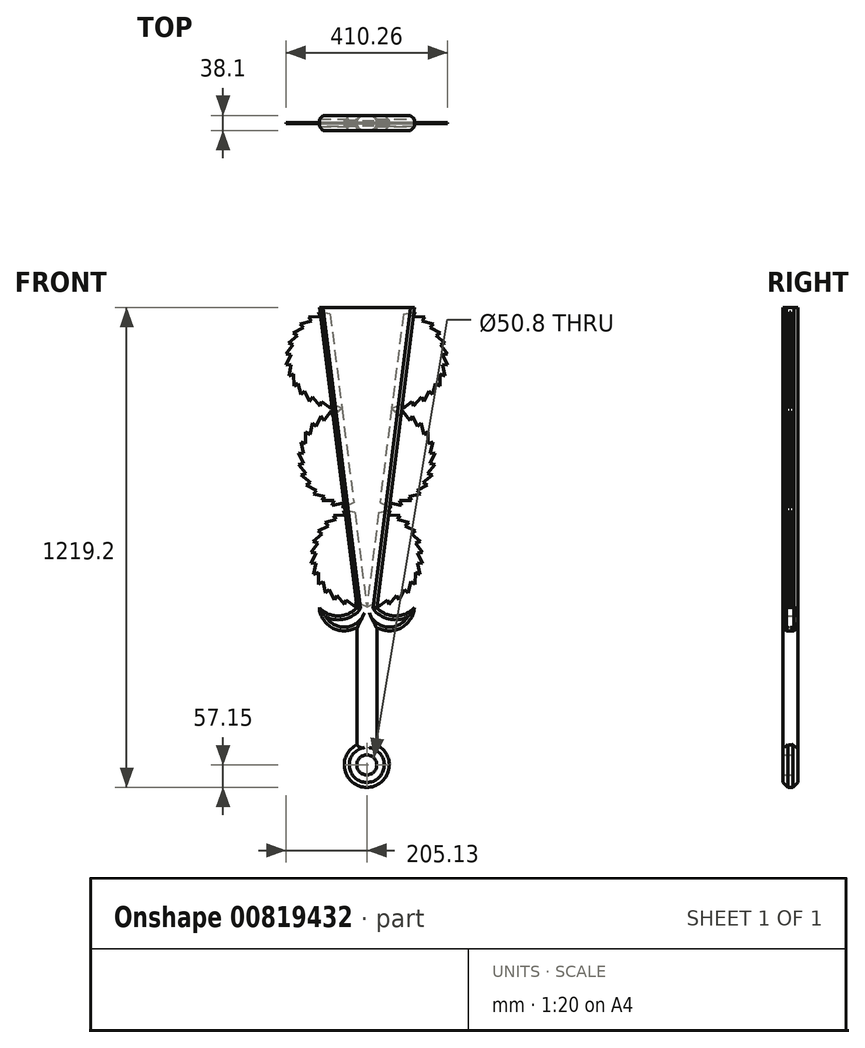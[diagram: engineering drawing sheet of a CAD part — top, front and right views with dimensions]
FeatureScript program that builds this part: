
annotation { "Feature Type Name" : "Feature", "Feature Type Description" : "" }
export const myFeature = defineFeature(function(context is Context, id is Id, definition is map)
    precondition{}
    {
        {
            var Q0;
            Q0=qCreatedBy(makeId("Front.planeOp"),FACE);
            var sketch = newSketch(context, id + "F0", { "sketchPlane" : qUnion([Q0])});
            skLineSegment(sketch, "E0.bottom", {"start": v(120.65, 0) * mm, "end": v(-120.65, 0) * mm});
            skLineSegment(sketch, "E0.top", {"start": v(120.65, 1219.2) * mm, "end": v(-120.65, 1219.2) * mm});
            skLineSegment(sketch, "E0.left", {"start": v(120.65, 0) * mm, "end": v(120.65, 1219.2) * mm});
            skLineSegment(sketch, "E0.right", {"start": v(-120.65, 0) * mm, "end": v(-120.65, 1219.2) * mm});
            skPoint(sketch, "E0.middle", {"position": v(0, 609.6) * mm});
            skLineSegment(sketch, "E1", {"start": v(-25.4, 457.2) * mm, "end": v(25.4, 457.2) * mm, "construction": true});
            skLineSegment(sketch, "E2.bottom", {"start": v(25.4, 457.2) * mm, "end": v(-25.4, 457.2) * mm, "construction": true});
            skLineSegment(sketch, "E2.top", {"start": v(25.4, 0) * mm, "end": v(-25.4, 0) * mm, "construction": true});
            skLineSegment(sketch, "E2.left", {"start": v(25.4, 457.2) * mm, "end": v(25.4, 0) * mm, "construction": true});
            skLineSegment(sketch, "E2.right", {"start": v(-25.4, 457.2) * mm, "end": v(-25.4, 0) * mm, "construction": true});
            skPoint(sketch, "E2.middle", {"position": v(0, 228.6) * mm});
            skArc(sketch, "E3", {"start": v(-25.4, 108.35) * mm, "mid": v(0, 0) * mm, "end": v(25.4, 108.35) * mm});
            skLineSegment(sketch, "E4", {"start": v(-25.4, 406.4) * mm, "end": v(-25.4, 108.35) * mm});
            skLineSegment(sketch, "E5", {"start": v(25.4, 406.4) * mm, "end": v(25.4, 108.35) * mm});
            skCircle(sketch, "E6", {"center": v(0, 57.15) * mm, "radius": 25.4 * mm});
            skPoint(sketch, "E7.end.orphan", {"position": v(120.65, 457.2) * mm});
            skLineSegment(sketch, "E8", {"start": v(-120.65, 1219.2) * mm, "end": v(-25.4, 457.2) * mm});
            skLineSegment(sketch, "E9", {"start": v(120.65, 1219.2) * mm, "end": v(25.4, 457.2) * mm});
            skLineSegment(sketch, "E10", {"start": v(-120.65, 457.2) * mm, "end": v(120.65, 457.2) * mm, "construction": true});
            skArc(sketch, "E11", {"start": v(25.4, 457.2) * mm, "mid": v(73.03, 435.7) * mm, "end": v(120.65, 457.2) * mm});
            skArc(sketch, "E12", {"start": v(120.65, 457.2) * mm, "mid": v(87.17, 405.29) * mm, "end": v(25.4, 406.4) * mm});
            skLineSegment(sketch, "E13", {"start": v(0, -278.18) * mm, "end": v(0, 1875.85) * mm, "construction": true});
            skArc(sketch, "E14.MirrorCS", {"start": v(-25.4, 457.2) * mm, "mid": v(-73.03, 435.7) * mm, "end": v(-120.65, 457.2) * mm});
            skArc(sketch, "E15.MirrorCS", {"start": v(-120.65, 457.2) * mm, "mid": v(-87.17, 405.29) * mm, "end": v(-25.4, 406.4) * mm});
            skSolve(sketch);
        }
        {
            var Q0;
            {var subQ1=sQuery(id+"F0.wireOp",EDGE,"E0.top");Q0=makeQuery(id+"F0.imprint","IMPRINT",FACE,{"disambiguationData":[TD([[makeQuery(id+"F0.imprint","IMPRINT",EDGE,{"derivedFrom":subQ1}),1.0]])]});}
            extrude(context, id + "F1", {"entities" : qUnion([Q0]), "depth" : 19.05 * mm, "offsetDistance" : 25.4 * mm, "hasSecondDirection" : true, "secondDirectionOppositeDirection" : true, "secondDirectionDepth" : 19.05 * mm});
        }
        {
            var Q0;
            Q0=makeQuery(id+"F0.imprint","IMPRINT",FACE,{"disambiguationData":[TD([[makeQuery(id+"F0.imprint","IMPRINT",EDGE,{"derivedFrom":sQuery(id+"F0.wireOp",EDGE,"E6")}),1.0]])]});
            extrude(context, id + "F2", {"entities" : qUnion([Q0]), "depth" : 19.05 * mm, "offsetDistance" : 25.4 * mm, "hasSecondDirection" : true, "secondDirectionOppositeDirection" : true, "secondDirectionDepth" : 19.05 * mm});
        }
        {
            var Q0;
            Q0=makeQuery(id+"F1.opExtrude","CAP_EDGE",EDGE,{"disambiguationData":[OSD([sQuery(id+"F0.wireOp",EDGE,"E4")])],"isStart":false});
            var Q1;
            Q1=makeQuery(id+"F1.opExtrude","CAP_EDGE",EDGE,{"disambiguationData":[OSD([sQuery(id+"F0.wireOp",EDGE,"E4")])],"isStart":true});
            var Q2;
            Q2=makeQuery(id+"F1.opExtrude","CAP_EDGE",EDGE,{"disambiguationData":[OSD([sQuery(id+"F0.wireOp",EDGE,"E5")])],"isStart":false});
            var Q3;
            Q3=makeQuery(id+"F1.opExtrude","CAP_EDGE",EDGE,{"disambiguationData":[OSD([sQuery(id+"F0.wireOp",EDGE,"E5")])],"isStart":true});
            fillet(context, id + "F3", {"entities" : qUnion([Q0, Q1, Q2, Q3]), "radius" : 19.05 * mm, "tangentPropagation" : true, "allowEdgeOverflow" : false});
        }
        {
            var Q0;
            Q0=makeQuery(id+"F1.opExtrude","CAP_EDGE",EDGE,{"disambiguationData":[OSD([sQuery(id+"F0.wireOp",EDGE,"E3")])],"isStart":false});
            var Q1;
            Q1=makeQuery(id+"F1.opExtrude","CAP_EDGE",EDGE,{"disambiguationData":[OSD([sQuery(id+"F0.wireOp",EDGE,"E3")])],"isStart":true});
            chamfer(context, id + "F4", {"entities" : qUnion([Q0, Q1]), "width" : 12.7 * mm, "tangentPropagation" : true});
        }
        {
            var Q0;
            Q0=qCreatedBy(makeId("Front.planeOp"),FACE);
            var sketch = newSketch(context, id + "F5", { "sketchPlane" : qUnion([Q0])});
            skLineSegment(sketch, "E16.bottom", {"start": v(120.65, 457.2) * mm, "end": v(-120.65, 457.2) * mm, "construction": true});
            skLineSegment(sketch, "E16.top", {"start": v(120.65, 1219.2) * mm, "end": v(-120.65, 1219.2) * mm, "construction": true});
            skLineSegment(sketch, "E16.left", {"start": v(120.65, 457.2) * mm, "end": v(120.65, 1219.2) * mm, "construction": true});
            skLineSegment(sketch, "E16.right", {"start": v(-120.65, 457.2) * mm, "end": v(-120.65, 1219.2) * mm, "construction": true});
            skPoint(sketch, "E16.middle", {"position": v(0, 838.2) * mm});
            skLineSegment(sketch, "E17", {"start": v(120.65, 1219.2) * mm, "end": v(25.4, 457.2) * mm, "construction": true});
            skLineSegment(sketch, "E18", {"start": v(-25.4, 457.2) * mm, "end": v(-120.65, 1219.2) * mm, "construction": true});
            skLineSegment(sketch, "E19", {"start": v(95.05, 1219.2) * mm, "end": v(-0.2, 457.2) * mm});
            skLineSegment(sketch, "E20", {"start": v(0.2, 457.2) * mm, "end": v(-95.05, 1219.2) * mm, "construction": true});
            skArc(sketch, "E21", {"start": v(0, 458.78) * mm, "mid": v(141.77, 569.05) * mm, "end": v(31.5, 710.82) * mm, "construction": true});
            skLineSegment(sketch, "E22", {"start": v(0, -215.51) * mm, "end": v(0, 1906.29) * mm, "construction": true});
            skArc(sketch, "E23", {"start": v(31.5, 710.82) * mm, "mid": v(173.28, 821.09) * mm, "end": v(63, 962.86) * mm, "construction": true});
            skArc(sketch, "E24", {"start": v(63, 962.86) * mm, "mid": v(204.78, 1073.13) * mm, "end": v(94.51, 1214.9) * mm, "construction": true});
            skPoint(sketch, "E25", {"position": v(0, 458.78) * mm});
            skLineSegment(sketch, "E26", {"start": v(15.75, 584.8) * mm, "end": v(120.65, 571.69) * mm, "construction": true});
            skLineSegment(sketch, "E27", {"start": v(47.26, 836.84) * mm, "end": v(173.28, 821.09) * mm, "construction": true});
            skLineSegment(sketch, "E28", {"start": v(78.76, 1088.88) * mm, "end": v(204.78, 1073.13) * mm, "construction": true});
            skLineSegment(sketch, "E29", {"start": v(15.75, 584.8) * mm, "end": v(120.65, 546.66) * mm, "construction": true});
            skLineSegment(sketch, "E30", {"start": v(15.75, 584.8) * mm, "end": v(39.44, 569.51) * mm, "construction": true});
            skLineSegment(sketch, "E31", {"start": v(104.46, 493.91) * mm, "end": v(95.59, 503) * mm});
            skLineSegment(sketch, "E32", {"start": v(82, 476.45) * mm, "end": v(75.38, 487.29) * mm});
            skLineSegment(sketch, "E33", {"start": v(56.24, 464.43) * mm, "end": v(52.2, 476.46) * mm});
            skLineSegment(sketch, "E34", {"start": v(28.44, 458.44) * mm, "end": v(27.15, 471.23) * mm});
            skLineSegment(sketch, "E35", {"start": v(142.12, 597.48) * mm, "end": v(129.48, 596.22) * mm});
            skLineSegment(sketch, "E36", {"start": v(136.13, 625.29) * mm, "end": v(124.09, 621.24) * mm});
            skLineSegment(sketch, "E37", {"start": v(124.1, 651.06) * mm, "end": v(113.27, 644.43) * mm});
            skLineSegment(sketch, "E38", {"start": v(106.64, 673.5) * mm, "end": v(97.55, 664.63) * mm});
            skLineSegment(sketch, "E39", {"start": v(84.62, 691.5) * mm, "end": v(77.74, 680.83) * mm});
            skLineSegment(sketch, "E40", {"start": v(59.15, 704.15) * mm, "end": v(54.81, 692.22) * mm});
            skLineSegment(sketch, "E41", {"start": v(31.5, 710.82) * mm, "end": v(258.62, 682.43) * mm, "construction": true});
            skLineSegment(sketch, "E42", {"start": v(63, 962.86) * mm, "end": v(273.36, 936.56) * mm, "construction": true});
            skLineSegment(sketch, "E43", {"start": v(52.2, 476.46) * mm, "end": v(28.44, 458.44) * mm});
            skLineSegment(sketch, "E44", {"start": v(75.38, 487.29) * mm, "end": v(56.24, 464.43) * mm});
            skLineSegment(sketch, "E45", {"start": v(95.59, 503) * mm, "end": v(82, 476.45) * mm});
            skLineSegment(sketch, "E46", {"start": v(111.79, 522.82) * mm, "end": v(104.46, 493.91) * mm});
            skLineSegment(sketch, "E47", {"start": v(123.17, 545.74) * mm, "end": v(122.46, 515.93) * mm});
            skLineSegment(sketch, "E48", {"start": v(129.17, 570.62) * mm, "end": v(135.1, 541.4) * mm});
            skLineSegment(sketch, "E49", {"start": v(129.48, 596.22) * mm, "end": v(141.77, 569.05) * mm});
            skLineSegment(sketch, "E50", {"start": v(124.09, 621.24) * mm, "end": v(142.12, 597.48) * mm});
            skLineSegment(sketch, "E51", {"start": v(113.27, 644.43) * mm, "end": v(136.13, 625.29) * mm});
            skLineSegment(sketch, "E52", {"start": v(97.55, 664.63) * mm, "end": v(124.1, 651.06) * mm});
            skLineSegment(sketch, "E53", {"start": v(77.74, 680.83) * mm, "end": v(106.64, 673.5) * mm});
            skLineSegment(sketch, "E54", {"start": v(54.81, 692.22) * mm, "end": v(84.62, 691.5) * mm});
            skLineSegment(sketch, "E55", {"start": v(29.93, 698.22) * mm, "end": v(59.15, 704.15) * mm});
            skLineSegment(sketch, "E56.trimOffspring", {"start": v(44.9, 613.25) * mm, "end": v(15.75, 584.8) * mm, "construction": true});
            skLineSegment(sketch, "E57.trimOffspring", {"start": v(47.5, 633.98) * mm, "end": v(15.75, 584.8) * mm, "construction": true});
            skLineSegment(sketch, "E58.trimOffspring", {"start": v(43.47, 601.75) * mm, "end": v(15.75, 584.8) * mm, "construction": true});
            skLineSegment(sketch, "E59.trimOffspring", {"start": v(120.65, 620.08) * mm, "end": v(15.75, 584.8) * mm, "construction": true});
            skLineSegment(sketch, "E60.trimOffspring", {"start": v(120.65, 595.33) * mm, "end": v(15.75, 584.8) * mm, "construction": true});
            skLineSegment(sketch, "E61.trimOffspring", {"start": v(129.17, 570.62) * mm, "end": v(141.77, 569.05) * mm});
            skLineSegment(sketch, "E62.trimOffspring", {"start": v(123.17, 545.74) * mm, "end": v(135.1, 541.4) * mm});
            skLineSegment(sketch, "E63.trimOffspring", {"start": v(111.79, 522.82) * mm, "end": v(122.46, 515.93) * mm});
            skLineSegment(sketch, "E64.trimOffspring", {"start": v(38.44, 561.55) * mm, "end": v(15.75, 584.8) * mm, "construction": true});
            skLineSegment(sketch, "E65.trimOffspring", {"start": v(37, 550.05) * mm, "end": v(15.75, 584.8) * mm, "construction": true});
            skLineSegment(sketch, "E66.trimOffspring", {"start": v(34.41, 529.32) * mm, "end": v(15.75, 584.8) * mm, "construction": true});
            skLineSegment(sketch, "E67", {"start": v(0, 458.78) * mm, "end": v(27.15, 471.23) * mm});
            skLineSegment(sketch, "E68.MirrorCS", {"start": v(63, 962.86) * mm, "end": v(86.26, 944.1) * mm});
            skLineSegment(sketch, "E69.MirrorCS", {"start": v(90.66, 956.2) * mm, "end": v(86.26, 944.1) * mm});
            skLineSegment(sketch, "E70.MirrorCS", {"start": v(116.13, 943.54) * mm, "end": v(109.24, 932.87) * mm});
            skLineSegment(sketch, "E71.MirrorCS", {"start": v(109.24, 932.87) * mm, "end": v(90.66, 956.2) * mm});
            skLineSegment(sketch, "E72.MirrorCS", {"start": v(129.06, 916.67) * mm, "end": v(116.13, 943.54) * mm});
            skLineSegment(sketch, "E73.MirrorCS", {"start": v(138.15, 925.54) * mm, "end": v(129.06, 916.67) * mm});
            skLineSegment(sketch, "E74.MirrorCS", {"start": v(144.77, 896.47) * mm, "end": v(138.15, 925.54) * mm});
            skLineSegment(sketch, "E75.MirrorCS", {"start": v(155.6, 903.1) * mm, "end": v(144.77, 896.47) * mm});
            skLineSegment(sketch, "E76.MirrorCS", {"start": v(155.6, 873.28) * mm, "end": v(155.6, 903.1) * mm});
            skLineSegment(sketch, "E77.MirrorCS", {"start": v(160.99, 848.25) * mm, "end": v(167.63, 877.32) * mm});
            skLineSegment(sketch, "E78.MirrorCS", {"start": v(160.99, 848.25) * mm, "end": v(173.62, 849.52) * mm});
            skLineSegment(sketch, "E79.MirrorCS", {"start": v(155.6, 873.28) * mm, "end": v(167.63, 877.32) * mm});
            skLineSegment(sketch, "E80.MirrorCS", {"start": v(160.67, 822.66) * mm, "end": v(173.62, 849.52) * mm});
            skLineSegment(sketch, "E81.MirrorCS", {"start": v(160.67, 822.66) * mm, "end": v(173.28, 821.09) * mm});
            skLineSegment(sketch, "E82.MirrorCS", {"start": v(154.68, 797.78) * mm, "end": v(173.28, 821.09) * mm});
            skLineSegment(sketch, "E83.MirrorCS", {"start": v(166.61, 793.44) * mm, "end": v(154.68, 797.78) * mm});
            skLineSegment(sketch, "E84.MirrorCS", {"start": v(143.3, 774.86) * mm, "end": v(166.61, 793.44) * mm});
            skLineSegment(sketch, "E85.MirrorCS", {"start": v(153.96, 767.97) * mm, "end": v(143.3, 774.86) * mm});
            skLineSegment(sketch, "E86.MirrorCS", {"start": v(127.1, 755.04) * mm, "end": v(153.96, 767.97) * mm});
            skLineSegment(sketch, "E87.MirrorCS", {"start": v(135.96, 745.95) * mm, "end": v(127.1, 755.04) * mm});
            skLineSegment(sketch, "E88.MirrorCS", {"start": v(106.89, 739.33) * mm, "end": v(135.96, 745.95) * mm});
            skLineSegment(sketch, "E89.MirrorCS", {"start": v(83.7, 728.5) * mm, "end": v(113.51, 728.5) * mm});
            skLineSegment(sketch, "E90.MirrorCS", {"start": v(58.67, 723.11) * mm, "end": v(87.74, 716.47) * mm});
            skLineSegment(sketch, "E91.MirrorCS", {"start": v(59.94, 710.47) * mm, "end": v(58.67, 723.11) * mm});
            skLineSegment(sketch, "E92.MirrorCS", {"start": v(33.08, 723.42) * mm, "end": v(59.94, 710.47) * mm});
            skLineSegment(sketch, "E93.MirrorCS", {"start": v(87.74, 716.47) * mm, "end": v(83.7, 728.5) * mm});
            skLineSegment(sketch, "E94.MirrorCS", {"start": v(113.51, 728.5) * mm, "end": v(106.89, 739.33) * mm});
            skLineSegment(sketch, "E95.MirrorCS", {"start": v(92.94, 1202.3) * mm, "end": v(122.16, 1208.23) * mm});
            skLineSegment(sketch, "E96.MirrorCS", {"start": v(122.16, 1208.23) * mm, "end": v(117.82, 1196.3) * mm});
            skLineSegment(sketch, "E97.MirrorCS", {"start": v(117.82, 1196.3) * mm, "end": v(147.63, 1195.58) * mm});
            skLineSegment(sketch, "E98.MirrorCS", {"start": v(140.75, 1184.91) * mm, "end": v(169.65, 1177.58) * mm});
            skLineSegment(sketch, "E99.MirrorCS", {"start": v(147.63, 1195.58) * mm, "end": v(140.75, 1184.91) * mm});
            skLineSegment(sketch, "E100.MirrorCS", {"start": v(169.65, 1177.58) * mm, "end": v(160.56, 1168.71) * mm});
            skLineSegment(sketch, "E101.MirrorCS", {"start": v(160.56, 1168.71) * mm, "end": v(187.1, 1155.13) * mm});
            skLineSegment(sketch, "E102.MirrorCS", {"start": v(176.28, 1148.5) * mm, "end": v(199.14, 1129.36) * mm});
            skLineSegment(sketch, "E103.MirrorCS", {"start": v(187.1, 1125.31) * mm, "end": v(205.13, 1101.56) * mm});
            skLineSegment(sketch, "E104.MirrorCS", {"start": v(205.13, 1101.56) * mm, "end": v(192.5, 1100.3) * mm});
            skLineSegment(sketch, "E105.MirrorCS", {"start": v(192.5, 1100.3) * mm, "end": v(204.78, 1073.13) * mm});
            skLineSegment(sketch, "E106.MirrorCS", {"start": v(199.14, 1129.36) * mm, "end": v(187.1, 1125.31) * mm});
            skLineSegment(sketch, "E107.MirrorCS", {"start": v(187.1, 1155.13) * mm, "end": v(176.28, 1148.5) * mm});
            skLineSegment(sketch, "E108.MirrorCS", {"start": v(192.18, 1074.7) * mm, "end": v(204.78, 1073.13) * mm});
            skLineSegment(sketch, "E109.MirrorCS", {"start": v(192.18, 1074.7) * mm, "end": v(198.12, 1045.48) * mm});
            skLineSegment(sketch, "E110.MirrorCS", {"start": v(186.18, 1049.82) * mm, "end": v(198.12, 1045.48) * mm});
            skLineSegment(sketch, "E111.MirrorCS", {"start": v(186.18, 1049.82) * mm, "end": v(185.47, 1020) * mm});
            skLineSegment(sketch, "E112.MirrorCS", {"start": v(174.8, 1026.9) * mm, "end": v(185.47, 1020) * mm});
            skLineSegment(sketch, "E113.MirrorCS", {"start": v(174.8, 1026.9) * mm, "end": v(167.47, 998) * mm});
            skLineSegment(sketch, "E114.MirrorCS", {"start": v(158.6, 1007.08) * mm, "end": v(145.02, 980.53) * mm});
            skLineSegment(sketch, "E115.MirrorCS", {"start": v(167.47, 998) * mm, "end": v(158.6, 1007.08) * mm});
            skLineSegment(sketch, "E116.MirrorCS", {"start": v(145.02, 980.53) * mm, "end": v(138.4, 991.37) * mm});
            skLineSegment(sketch, "E117.MirrorCS", {"start": v(138.4, 991.37) * mm, "end": v(119.25, 968.5) * mm});
            skLineSegment(sketch, "E118.MirrorCS", {"start": v(119.25, 968.5) * mm, "end": v(115.2, 980.54) * mm});
            skLineSegment(sketch, "E119.MirrorCS", {"start": v(115.2, 980.54) * mm, "end": v(91.45, 962.51) * mm});
            skLineSegment(sketch, "E120.MirrorCS", {"start": v(91.45, 962.51) * mm, "end": v(90.16, 975.3) * mm});
            skLineSegment(sketch, "E121.MirrorCS", {"start": v(63, 962.86) * mm, "end": v(90.16, 975.3) * mm});
            skSolve(sketch);
        }
        {
            var Q0;
            Q0=makeQuery(id+"F1.opExtrude","CAP_EDGE",EDGE,{"disambiguationData":[OSD([sQuery(id+"F0.wireOp",EDGE,"E12")])],"isStart":false});
            var Q1;
            Q1=makeQuery(id+"F1.opExtrude","CAP_EDGE",EDGE,{"disambiguationData":[OSD([sQuery(id+"F0.wireOp",EDGE,"E12")])],"isStart":true});
            var Q2;
            Q2=makeQuery(id+"F1.opExtrude","CAP_EDGE",EDGE,{"disambiguationData":[OSD([sQuery(id+"F0.wireOp",EDGE,"E15.MirrorCS")])],"isStart":true});
            var Q3;
            Q3=makeQuery(id+"F1.opExtrude","CAP_EDGE",EDGE,{"disambiguationData":[OSD([sQuery(id+"F0.wireOp",EDGE,"E15.MirrorCS")])],"isStart":false});
            var Q4;
            Q4=makeQuery(id+"F1.opExtrude","CAP_EDGE",EDGE,{"disambiguationData":[OSD([sQuery(id+"F0.wireOp",EDGE,"E14.MirrorCS")])],"isStart":false});
            var Q5;
            Q5=makeQuery(id+"F1.opExtrude","CAP_EDGE",EDGE,{"disambiguationData":[OSD([sQuery(id+"F0.wireOp",EDGE,"E14.MirrorCS")])],"isStart":true});
            var Q6;
            Q6=makeQuery(id+"F1.opExtrude","CAP_EDGE",EDGE,{"disambiguationData":[OSD([sQuery(id+"F0.wireOp",EDGE,"E11")])],"isStart":false});
            var Q7;
            Q7=makeQuery(id+"F1.opExtrude","CAP_EDGE",EDGE,{"disambiguationData":[OSD([sQuery(id+"F0.wireOp",EDGE,"E11")])],"isStart":true});
            var Q8;
            Q8=makeQuery(id+"F1.opExtrude","CAP_EDGE",EDGE,{"disambiguationData":[OSD([sQuery(id+"F0.wireOp",EDGE,"E9")])],"isStart":false});
            var Q9;
            Q9=makeQuery(id+"F1.opExtrude","CAP_EDGE",EDGE,{"disambiguationData":[OSD([sQuery(id+"F0.wireOp",EDGE,"E9")])],"isStart":true});
            var Q10;
            Q10=makeQuery(id+"F1.opExtrude","CAP_EDGE",EDGE,{"disambiguationData":[OSD([sQuery(id+"F0.wireOp",EDGE,"E8")])],"isStart":false});
            var Q11;
            Q11=makeQuery(id+"F1.opExtrude","CAP_EDGE",EDGE,{"disambiguationData":[OSD([sQuery(id+"F0.wireOp",EDGE,"E8")])],"isStart":true});
            chamfer(context, id + "F6", {"entities" : qUnion([Q0, Q1, Q2, Q3, Q4, Q5, Q6, Q7, Q8, Q9, Q10, Q11]), "width" : 9.52 * mm});
        }
        {
            var Q0;
            {var subQ0=sQuery(id+"F5.wireOp",EDGE,"E68.MirrorCS");Q0=makeQuery(id+"F5.imprint","IMPRINT",FACE,{"disambiguationData":[TD([[makeQuery(id+"F5.imprint","IMPRINT",EDGE,{"derivedFrom":subQ0}),-1.0]])]});}
            var Q1;
            {var subQ0=sQuery(id+"F5.wireOp",EDGE,"E95.MirrorCS");Q1=makeQuery(id+"F5.imprint","IMPRINT",FACE,{"disambiguationData":[TD([[makeQuery(id+"F5.imprint","IMPRINT",EDGE,{"derivedFrom":subQ0}),-1.0]])]});}
            var Q2;
            Q2=makeQuery(id+"F5.imprint","IMPRINT",FACE,{"disambiguationData":[TD([[makeQuery(id+"F5.imprint","IMPRINT",EDGE,{"derivedFrom":sQuery(id+"F5.wireOp",EDGE,"E31")}),-1.0]])]});
            extrude(context, id + "F7", {"entities" : qUnion([Q0, Q1, Q2]), "depth" : 1.59 * mm, "offsetDistance" : 25.4 * mm, "hasSecondDirection" : true, "secondDirectionOppositeDirection" : true, "secondDirectionDepth" : 1.59 * mm});
        }
        {
            var Q0;
            Q0=makeQuery(id+"F7.opExtrude","SWEPT_BODY",BODY,{"disambiguationData":[OSD([sQuery(id+"F5.wireOp",EDGE,"E19"),sQuery(id+"F5.wireOp",EDGE,"E31"),sQuery(id+"F5.wireOp",EDGE,"E32"),sQuery(id+"F5.wireOp",EDGE,"E34"),sQuery(id+"F5.wireOp",EDGE,"E35"),sQuery(id+"F5.wireOp",EDGE,"E36"),sQuery(id+"F5.wireOp",EDGE,"E37"),sQuery(id+"F5.wireOp",EDGE,"E38"),sQuery(id+"F5.wireOp",EDGE,"E39"),sQuery(id+"F5.wireOp",EDGE,"E40"),sQuery(id+"F5.wireOp",EDGE,"E43"),sQuery(id+"F5.wireOp",EDGE,"E44"),sQuery(id+"F5.wireOp",EDGE,"E45"),sQuery(id+"F5.wireOp",EDGE,"E46"),sQuery(id+"F5.wireOp",EDGE,"E47"),sQuery(id+"F5.wireOp",EDGE,"E48"),sQuery(id+"F5.wireOp",EDGE,"E49"),sQuery(id+"F5.wireOp",EDGE,"E50"),sQuery(id+"F5.wireOp",EDGE,"E51"),sQuery(id+"F5.wireOp",EDGE,"E52"),sQuery(id+"F5.wireOp",EDGE,"E53"),sQuery(id+"F5.wireOp",EDGE,"E54"),sQuery(id+"F5.wireOp",EDGE,"E55"),sQuery(id+"F5.wireOp",EDGE,"E61.trimOffspring"),sQuery(id+"F5.wireOp",EDGE,"E62.trimOffspring"),sQuery(id+"F5.wireOp",EDGE,"E63.trimOffspring"),sQuery(id+"F5.wireOp",EDGE,"E67"),sQuery(id+"F5.wireOp",EDGE,"E33")])]});
            var Q1;
            Q1=makeQuery(id+"F7.opExtrude","SWEPT_BODY",BODY,{"disambiguationData":[OSD([sQuery(id+"F5.wireOp",EDGE,"E19"),sQuery(id+"F5.wireOp",EDGE,"E68.MirrorCS"),sQuery(id+"F5.wireOp",EDGE,"E69.MirrorCS"),sQuery(id+"F5.wireOp",EDGE,"E70.MirrorCS"),sQuery(id+"F5.wireOp",EDGE,"E71.MirrorCS"),sQuery(id+"F5.wireOp",EDGE,"E72.MirrorCS"),sQuery(id+"F5.wireOp",EDGE,"E73.MirrorCS"),sQuery(id+"F5.wireOp",EDGE,"E74.MirrorCS"),sQuery(id+"F5.wireOp",EDGE,"E75.MirrorCS"),sQuery(id+"F5.wireOp",EDGE,"E76.MirrorCS"),sQuery(id+"F5.wireOp",EDGE,"E79.MirrorCS"),sQuery(id+"F5.wireOp",EDGE,"E77.MirrorCS"),sQuery(id+"F5.wireOp",EDGE,"E78.MirrorCS"),sQuery(id+"F5.wireOp",EDGE,"E80.MirrorCS"),sQuery(id+"F5.wireOp",EDGE,"E81.MirrorCS"),sQuery(id+"F5.wireOp",EDGE,"E82.MirrorCS"),sQuery(id+"F5.wireOp",EDGE,"E83.MirrorCS"),sQuery(id+"F5.wireOp",EDGE,"E84.MirrorCS"),sQuery(id+"F5.wireOp",EDGE,"E85.MirrorCS"),sQuery(id+"F5.wireOp",EDGE,"E86.MirrorCS"),sQuery(id+"F5.wireOp",EDGE,"E87.MirrorCS"),sQuery(id+"F5.wireOp",EDGE,"E88.MirrorCS"),sQuery(id+"F5.wireOp",EDGE,"E89.MirrorCS"),sQuery(id+"F5.wireOp",EDGE,"E90.MirrorCS"),sQuery(id+"F5.wireOp",EDGE,"E91.MirrorCS"),sQuery(id+"F5.wireOp",EDGE,"E92.MirrorCS"),sQuery(id+"F5.wireOp",EDGE,"E93.MirrorCS"),sQuery(id+"F5.wireOp",EDGE,"E94.MirrorCS")])]});
            var Q2;
            Q2=makeQuery(id+"F7.opExtrude","SWEPT_BODY",BODY,{"disambiguationData":[OSD([sQuery(id+"F5.wireOp",EDGE,"E19"),sQuery(id+"F5.wireOp",EDGE,"E95.MirrorCS"),sQuery(id+"F5.wireOp",EDGE,"E96.MirrorCS"),sQuery(id+"F5.wireOp",EDGE,"E97.MirrorCS"),sQuery(id+"F5.wireOp",EDGE,"E98.MirrorCS"),sQuery(id+"F5.wireOp",EDGE,"E99.MirrorCS"),sQuery(id+"F5.wireOp",EDGE,"E100.MirrorCS"),sQuery(id+"F5.wireOp",EDGE,"E101.MirrorCS"),sQuery(id+"F5.wireOp",EDGE,"E102.MirrorCS"),sQuery(id+"F5.wireOp",EDGE,"E103.MirrorCS"),sQuery(id+"F5.wireOp",EDGE,"E104.MirrorCS"),sQuery(id+"F5.wireOp",EDGE,"E106.MirrorCS"),sQuery(id+"F5.wireOp",EDGE,"E107.MirrorCS"),sQuery(id+"F5.wireOp",EDGE,"E105.MirrorCS"),sQuery(id+"F5.wireOp",EDGE,"E108.MirrorCS"),sQuery(id+"F5.wireOp",EDGE,"E109.MirrorCS"),sQuery(id+"F5.wireOp",EDGE,"E110.MirrorCS"),sQuery(id+"F5.wireOp",EDGE,"E111.MirrorCS"),sQuery(id+"F5.wireOp",EDGE,"E112.MirrorCS"),sQuery(id+"F5.wireOp",EDGE,"E113.MirrorCS"),sQuery(id+"F5.wireOp",EDGE,"E114.MirrorCS"),sQuery(id+"F5.wireOp",EDGE,"E115.MirrorCS"),sQuery(id+"F5.wireOp",EDGE,"E116.MirrorCS"),sQuery(id+"F5.wireOp",EDGE,"E117.MirrorCS"),sQuery(id+"F5.wireOp",EDGE,"E118.MirrorCS"),sQuery(id+"F5.wireOp",EDGE,"E119.MirrorCS"),sQuery(id+"F5.wireOp",EDGE,"E120.MirrorCS"),sQuery(id+"F5.wireOp",EDGE,"E121.MirrorCS")])]});
            var Q3;
            Q3=qCreatedBy(makeId("Right.planeOp"),FACE);
            mirror(context, id + "F8", {"entities" : qUnion([Q0, Q1, Q2]), "mirrorPlane" : qUnion([Q3])});
        }
    });
